# Revit family: MTXTYP002
name_source: partatom
category: Furniture
units: mm (PartAtom-declared; Revit-internal decimal feet)

## family parameters
Always vertical = Yes
Cut with Voids When Loaded = No
OmniClass Number = 23.40.20.00
OmniClass Title = General Furniture and Specialties
Render Appearance Source = Family Geometry
Room Calculation Point = No
Shared = No
Work Plane-Based = No

## types (1)
- MTXTYP002
    Cost = 51251 $
    Default Elevation = 0 mm  [stored 0 ft]
    Description = 2 x 57 in. Electrical Jumper  (Pt 36E & Vt 48), 3 x Matrix White Duplex Outlet - Line 1, 2 x Matrix White Duplex Outlet - Line 2, 3 x Matrix White Duplex Outlet - Line 3, 3 x Matrix White Duplex Outlet - Line 4 - Dedicated, 1 x 18 in. Electrical Jumper  (Panel To Panel), 4 x Single Powerway Assembly - 36W - 8 wire, 4 circuit, 2 x Access Hole Cover, 1 x LH Receptacle Mounted Base Infeed - 72L - 8 Wire, 4 Circuit, 1 x Dual Electrical Tile - 8H X 36W, 11 x Quad Electrical Tile - 8H X 36W, 12 x Tackable Acoustical Tile - 32H x 36W, 32 x Tackable Acoustical Tile - 40H x 36W, 2 x 3-Way  90 Degree Connector - Linear Trim - 42H, 8 x Frame End Cap - Linear Trim - 42H, 22 x Panel Frame - Linear Trim - 42H x 36W, 2 x 4-Way 90 Degree Connector - Linear Trim - 42H, 6 x Pedestal - B/B/F - 24D, 6 x Rectangular - 2mm Edge - 24D x 42W, 6 x Rectangular - 2mm Edge - 30D x 72W, 3 x O-LEG 27" X 30" MATRIX MOUNT LH, 3 x O-LEG 27" X 30" MATRIX MOUNT RH, 18 x Flat Plate, 3 x Regular Cantilever - Left Hand - 24D, 3 x Regular Cantilever - Right Hand - 24D, 3 x Regular Cantilever - Left Hand - 30D, 3 x Regular Cantilever - Right Hand - 30D, 6 x U-Channel - 48W, 18 x Rectangular Pull Handle with Paint Options
    Exported From CET Designer = Yes
    Manufacturer = AIS
    Model = E-MW8W4PJ36E
    Show MTXTYP002 = Yes
    VisibilityIndex = 0

note: [stored X ft] marks values corroborated as IEEE doubles in the binary element streams (Revit-internal decimal feet)

## geometry (parser evidence)
native form markers: Sweep x2
no freeform markers — native parametric forms only
